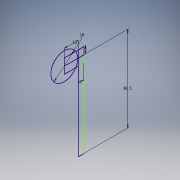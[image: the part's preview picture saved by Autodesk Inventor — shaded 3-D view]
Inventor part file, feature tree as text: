
AUTODESK INVENTOR PART (.ipt)
format: ipt  version: 2018 (Build 220112000, 112)  size: 92,672 bytes
history: native  units: in
note: dims shown in document units (in); Inventor stores cm internally (conversion verified against a paired STEP export)
features: sketch x1
ambient origin geometry x8: Origin, YZ Plane, XZ Plane, XY Plane, X Axis, Y Axis, Z Axis, Center Point
feature tree (1):
  sketch  "Sketch1"  dims[d0=0.748in d2=0.1969in d3=0.3937in d4=0.1575in d5=2.3819in]
